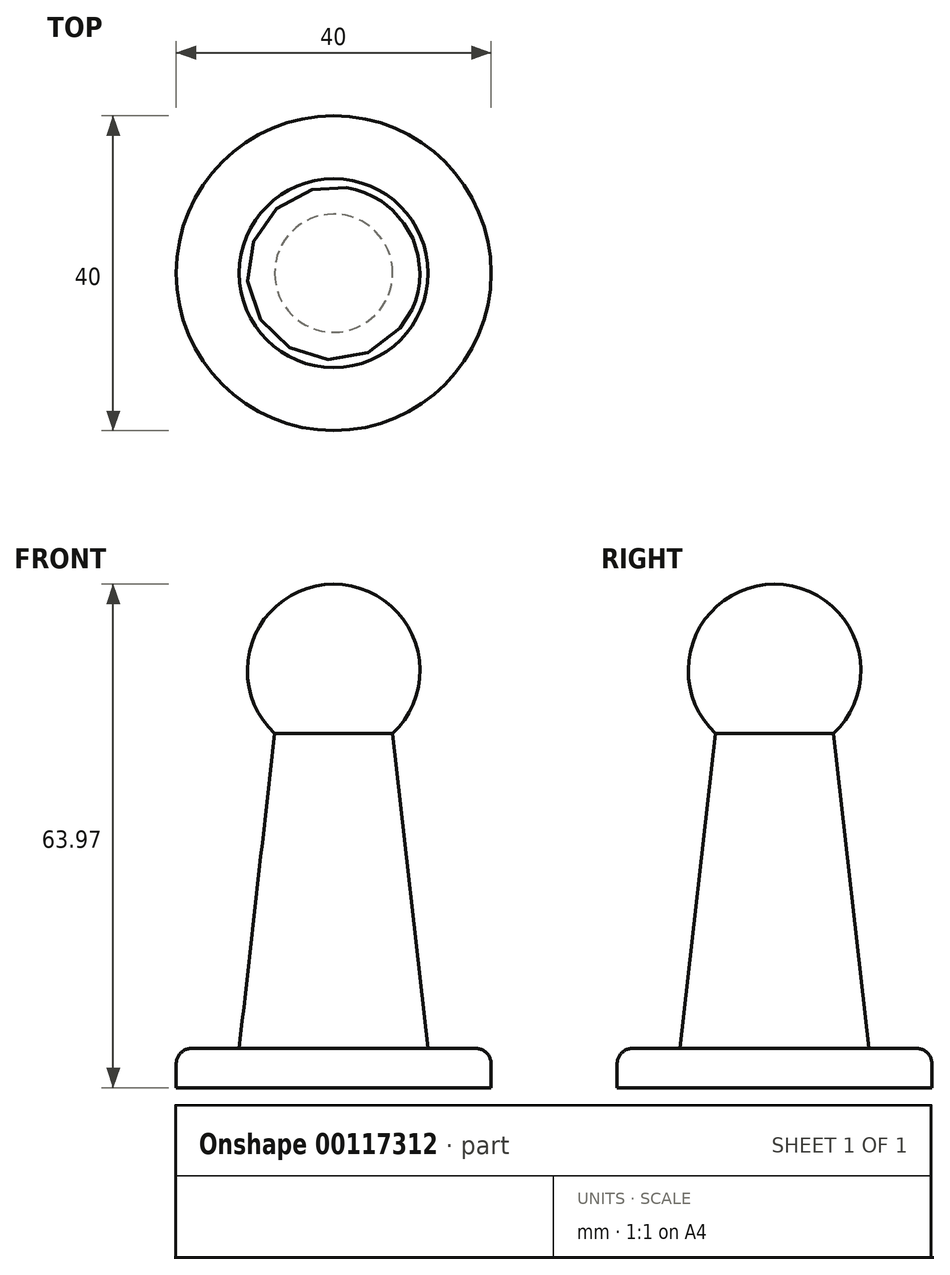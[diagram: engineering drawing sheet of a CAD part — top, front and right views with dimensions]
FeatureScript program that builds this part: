
annotation { "Feature Type Name" : "Feature", "Feature Type Description" : "" }
export const myFeature = defineFeature(function(context is Context, id is Id, definition is map)
    precondition{}
    {
        {
            var Q0;
            Q0=qCreatedBy(makeId("Front.planeOp"),FACE);
            var sketch = newSketch(context, id + "F0", { "sketchPlane" : qUnion([Q0])});
            skLineSegment(sketch, "E0.bottom", {"start": v(20, -2.5) * mm, "end": v(-20, -2.5) * mm, "construction": true});
            skLineSegment(sketch, "E0.top", {"start": v(20, 2.5) * mm, "end": v(-20, 2.5) * mm, "construction": true});
            skLineSegment(sketch, "E0.left", {"start": v(20, -2.5) * mm, "end": v(20, 2.5) * mm, "construction": true});
            skLineSegment(sketch, "E0.right", {"start": v(-20, -2.5) * mm, "end": v(-20, 2.5) * mm});
            skPoint(sketch, "E0.middle", {"position": v(0, 0) * mm});
            skLineSegment(sketch, "E1", {"start": v(-20, 2.5) * mm, "end": v(-12, 2.5) * mm});
            skLineSegment(sketch, "E2", {"start": v(20, 2.5) * mm, "end": v(12, 2.5) * mm, "construction": true});
            skLineSegment(sketch, "E3", {"start": v(0, 2.5) * mm, "end": v(0, 42.5) * mm, "construction": true});
            skLineSegment(sketch, "E4", {"start": v(0, 42.5) * mm, "end": v(7.5, 42.5) * mm, "construction": true});
            skLineSegment(sketch, "E5", {"start": v(0, 42.5) * mm, "end": v(-7.5, 42.5) * mm, "construction": true});
            skArc(sketch, "E6", {"start": v(7.5, 42.5) * mm, "mid": v(0, 61.47) * mm, "end": v(-7.5, 42.5) * mm, "construction": true});
            skLineSegment(sketch, "E7", {"start": v(-7.5, 42.5) * mm, "end": v(-12, 2.5) * mm});
            skLineSegment(sketch, "E8", {"start": v(7.5, 42.5) * mm, "end": v(12, 2.5) * mm, "construction": true});
            skLineSegment(sketch, "E9", {"start": v(0, -2.5) * mm, "end": v(0, 61.47) * mm});
            skArc(sketch, "E10", {"start": v(0, 61.47) * mm, "mid": v(-10.2, 54.53) * mm, "end": v(-7.5, 42.5) * mm});
            skLineSegment(sketch, "E11", {"start": v(-20, -2.5) * mm, "end": v(0, -2.5) * mm});
            skLineSegment(sketch, "E12", {"start": v(-7.5, 42.5) * mm, "end": v(-17.77, 52.13) * mm, "construction": true});
            skSolve(sketch);
        }
        {
            var Q0;
            Q0 = qSketchRegion(id + "F0", true);
            var Q1;
            Q1=sQuery(id+"F0.wireOp",EDGE,"E3");
            revolve(context, id + "F1", {"entities" : qUnion([Q0]), "axis" : qUnion([Q1]), "revolveType" : RevolveType.FULL});
        }
        {
            var Q0;
            Q0=makeQuery(id+"F1.opRevolve","SWEPT_EDGE",EDGE,{"disambiguationData":[OSD([sQuery(id+"F0.wireOp",EDGE,"E0.right"),sQuery(id+"F0.wireOp",EDGE,"E1")])]});
            fillet(context, id + "F2", {"entities" : qUnion([Q0]), "radius" : 2 * mm, "tangentPropagation" : true, "allowEdgeOverflow" : false});
        }
    });
